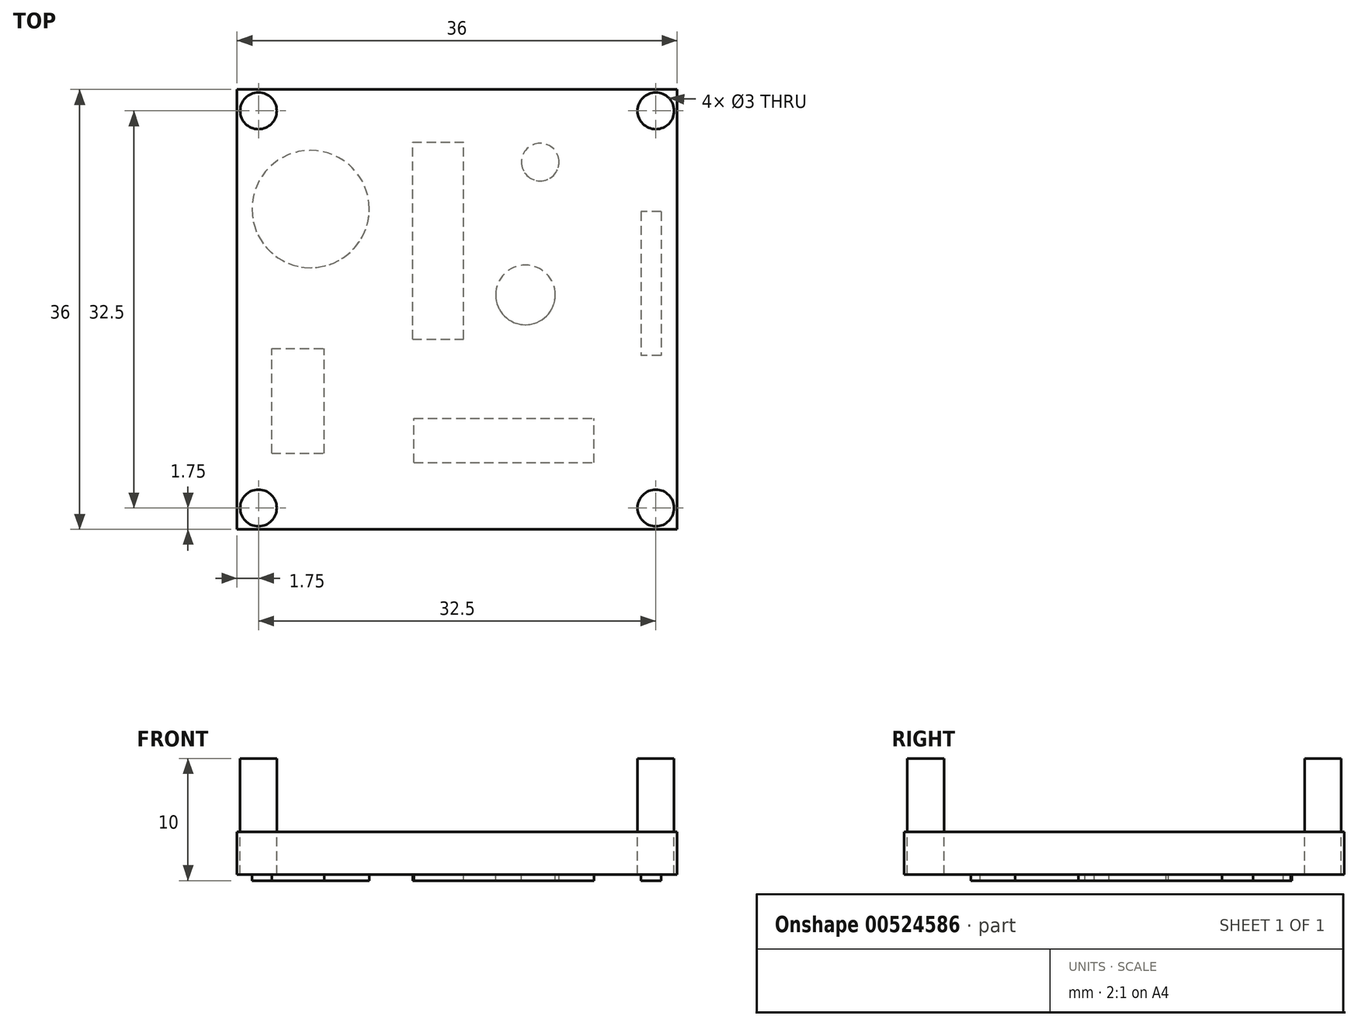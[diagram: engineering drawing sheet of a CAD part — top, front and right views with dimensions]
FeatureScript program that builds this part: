
annotation { "Feature Type Name" : "Feature", "Feature Type Description" : "" }
export const myFeature = defineFeature(function(context is Context, id is Id, definition is map)
    precondition{}
    {
        {
            var Q0;
            Q0=qCreatedBy(makeId("Top.planeOp"),FACE);
            var sketch = newSketch(context, id + "F0", { "sketchPlane" : qUnion([Q0])});
            skLineSegment(sketch, "E0.bottom", {"start": v(0, 0) * mm, "end": v(36, 0) * mm});
            skLineSegment(sketch, "E0.top", {"start": v(0, 36) * mm, "end": v(36, 36) * mm});
            skLineSegment(sketch, "E0.left", {"start": v(0, 0) * mm, "end": v(0, 36) * mm});
            skLineSegment(sketch, "E0.right", {"start": v(36, 0) * mm, "end": v(36, 36) * mm});
            skPoint(sketch, "E1", {"position": v(18, 1.75) * mm});
            skPoint(sketch, "E2", {"position": v(1.75, 18) * mm});
            skPoint(sketch, "E3", {"position": v(0, 18) * mm});
            skPoint(sketch, "E4", {"position": v(18, 0) * mm});
            skCircle(sketch, "E5", {"center": v(1.75, 34.25) * mm, "radius": 1.5 * mm});
            skCircle(sketch, "E6", {"center": v(34.25, 34.25) * mm, "radius": 1.5 * mm});
            skCircle(sketch, "E7", {"center": v(1.75, 1.75) * mm, "radius": 1.5 * mm});
            skCircle(sketch, "E8", {"center": v(34.25, 1.75) * mm, "radius": 1.5 * mm});
            skSolve(sketch);
        }
        {
            var Q0;
            Q0=makeQuery(id+"F0.imprint","IMPRINT",FACE,{"disambiguationData":[TD([[makeQuery(id+"F0.imprint","IMPRINT",EDGE,{"derivedFrom":sQuery(id+"F0.wireOp",EDGE,"E5")}),1.0]])]});
            var Q1;
            Q1=makeQuery(id+"F0.imprint","IMPRINT",FACE,{"disambiguationData":[TD([[makeQuery(id+"F0.imprint","IMPRINT",EDGE,{"derivedFrom":sQuery(id+"F0.wireOp",EDGE,"E6")}),1.0]])]});
            var Q2;
            Q2=makeQuery(id+"F0.imprint","IMPRINT",FACE,{"disambiguationData":[TD([[makeQuery(id+"F0.imprint","IMPRINT",EDGE,{"derivedFrom":sQuery(id+"F0.wireOp",EDGE,"E8")}),1.0]])]});
            var Q3;
            Q3=makeQuery(id+"F0.imprint","IMPRINT",FACE,{"disambiguationData":[TD([[makeQuery(id+"F0.imprint","IMPRINT",EDGE,{"derivedFrom":sQuery(id+"F0.wireOp",EDGE,"E7")}),1.0]])]});
            extrude(context, id + "F1", {"entities" : qUnion([Q0, Q1, Q2, Q3]), "depth" : 6 * mm, "offsetDistance" : 25 * mm});
        }
        {
            var Q0;
            Q0 = qSketchRegion(id + "F0", true);
            extrude(context, id + "F2", {"entities" : qUnion([Q0]), "oppositeDirection" : true, "depth" : 3.5 * mm, "offsetDistance" : 25 * mm});
        }
        {
            var Q0;
            Q0=makeQuery(id+"F2.opExtrude","CAP_FACE",FACE,{"disambiguationData":[OSD([sQuery(id+"F0.wireOp",EDGE,"E0.bottom"),sQuery(id+"F0.wireOp",EDGE,"E0.top"),sQuery(id+"F0.wireOp",EDGE,"E0.left"),sQuery(id+"F0.wireOp",EDGE,"E0.right"),sQuery(id+"F0.wireOp",EDGE,"E5"),sQuery(id+"F0.wireOp",EDGE,"E6"),sQuery(id+"F0.wireOp",EDGE,"E7"),sQuery(id+"F0.wireOp",EDGE,"E8")])],"isStart":false});
            var sketch = newSketch(context, id + "F3", { "sketchPlane" : qUnion([Q0])});
            skLineSegment(sketch, "E9.bottom", {"start": v(2.83, -6.22) * mm, "end": v(7.12, -6.22) * mm});
            skLineSegment(sketch, "E9.top", {"start": v(2.83, -14.8) * mm, "end": v(7.12, -14.8) * mm});
            skLineSegment(sketch, "E9.left", {"start": v(2.83, -6.22) * mm, "end": v(2.83, -14.8) * mm});
            skLineSegment(sketch, "E9.right", {"start": v(7.12, -6.22) * mm, "end": v(7.12, -14.8) * mm});
            skLineSegment(sketch, "E10.bottom", {"start": v(14.47, -5.46) * mm, "end": v(29.2, -5.46) * mm});
            skLineSegment(sketch, "E10.top", {"start": v(14.47, -9.08) * mm, "end": v(29.2, -9.08) * mm});
            skLineSegment(sketch, "E10.left", {"start": v(14.47, -5.46) * mm, "end": v(14.47, -9.08) * mm});
            skLineSegment(sketch, "E10.right", {"start": v(29.2, -5.46) * mm, "end": v(29.2, -9.08) * mm});
            skLineSegment(sketch, "E11.bottom", {"start": v(14.36, -15.56) * mm, "end": v(18.54, -15.56) * mm});
            skLineSegment(sketch, "E11.top", {"start": v(14.36, -31.7) * mm, "end": v(18.54, -31.7) * mm});
            skLineSegment(sketch, "E11.left", {"start": v(14.36, -15.56) * mm, "end": v(14.36, -31.7) * mm});
            skLineSegment(sketch, "E11.right", {"start": v(18.54, -15.56) * mm, "end": v(18.54, -31.7) * mm});
            skLineSegment(sketch, "E12.bottom", {"start": v(34.68, -26) * mm, "end": v(33.04, -26) * mm});
            skLineSegment(sketch, "E12.top", {"start": v(34.68, -14.24) * mm, "end": v(33.04, -14.24) * mm});
            skLineSegment(sketch, "E12.left", {"start": v(34.68, -26) * mm, "end": v(34.68, -14.24) * mm});
            skLineSegment(sketch, "E12.right", {"start": v(33.04, -26) * mm, "end": v(33.04, -14.24) * mm});
            skCircle(sketch, "E13", {"center": v(23.6, -19.18) * mm, "radius": 2.44 * mm});
            skCircle(sketch, "E14", {"center": v(24.8, -30.06) * mm, "radius": 1.54 * mm});
            skCircle(sketch, "E15", {"center": v(6.02, -26.21) * mm, "radius": 4.8 * mm});
            skSolve(sketch);
        }
        {
            var Q0;
            Q0=makeQuery(id+"F3.imprint","IMPRINT",FACE,{"disambiguationData":[TD([[makeQuery(id+"F3.imprint","IMPRINT",EDGE,{"derivedFrom":sQuery(id+"F3.wireOp",EDGE,"E9.bottom")}),-1.0]])]});
            var Q1;
            Q1=makeQuery(id+"F3.imprint","IMPRINT",FACE,{"disambiguationData":[TD([[makeQuery(id+"F3.imprint","IMPRINT",EDGE,{"derivedFrom":sQuery(id+"F3.wireOp",EDGE,"E10.bottom")}),-1.0]])]});
            var Q2;
            Q2=makeQuery(id+"F3.imprint","IMPRINT",FACE,{"disambiguationData":[TD([[makeQuery(id+"F3.imprint","IMPRINT",EDGE,{"derivedFrom":sQuery(id+"F3.wireOp",EDGE,"E13")}),1.0]])]});
            var Q3;
            Q3=makeQuery(id+"F3.imprint","IMPRINT",FACE,{"disambiguationData":[TD([[makeQuery(id+"F3.imprint","IMPRINT",EDGE,{"derivedFrom":sQuery(id+"F3.wireOp",EDGE,"E12.bottom")}),-1.0]])]});
            var Q4;
            Q4=makeQuery(id+"F3.imprint","IMPRINT",FACE,{"disambiguationData":[TD([[makeQuery(id+"F3.imprint","IMPRINT",EDGE,{"derivedFrom":sQuery(id+"F3.wireOp",EDGE,"E14")}),1.0]])]});
            var Q5;
            Q5=makeQuery(id+"F3.imprint","IMPRINT",FACE,{"disambiguationData":[TD([[makeQuery(id+"F3.imprint","IMPRINT",EDGE,{"derivedFrom":sQuery(id+"F3.wireOp",EDGE,"E11.bottom")}),-1.0]])]});
            var Q6;
            Q6=makeQuery(id+"F3.imprint","IMPRINT",FACE,{"disambiguationData":[TD([[makeQuery(id+"F3.imprint","IMPRINT",EDGE,{"derivedFrom":sQuery(id+"F3.wireOp",EDGE,"E15")}),1.0]])]});
            extrude(context, id + "F4", {"entities" : qUnion([Q0, Q1, Q2, Q3, Q4, Q5, Q6]), "operationType" : NewBodyOperationType.ADD, "depth" : .5 * mm, "offsetDistance" : 25 * mm});
        }
    });
